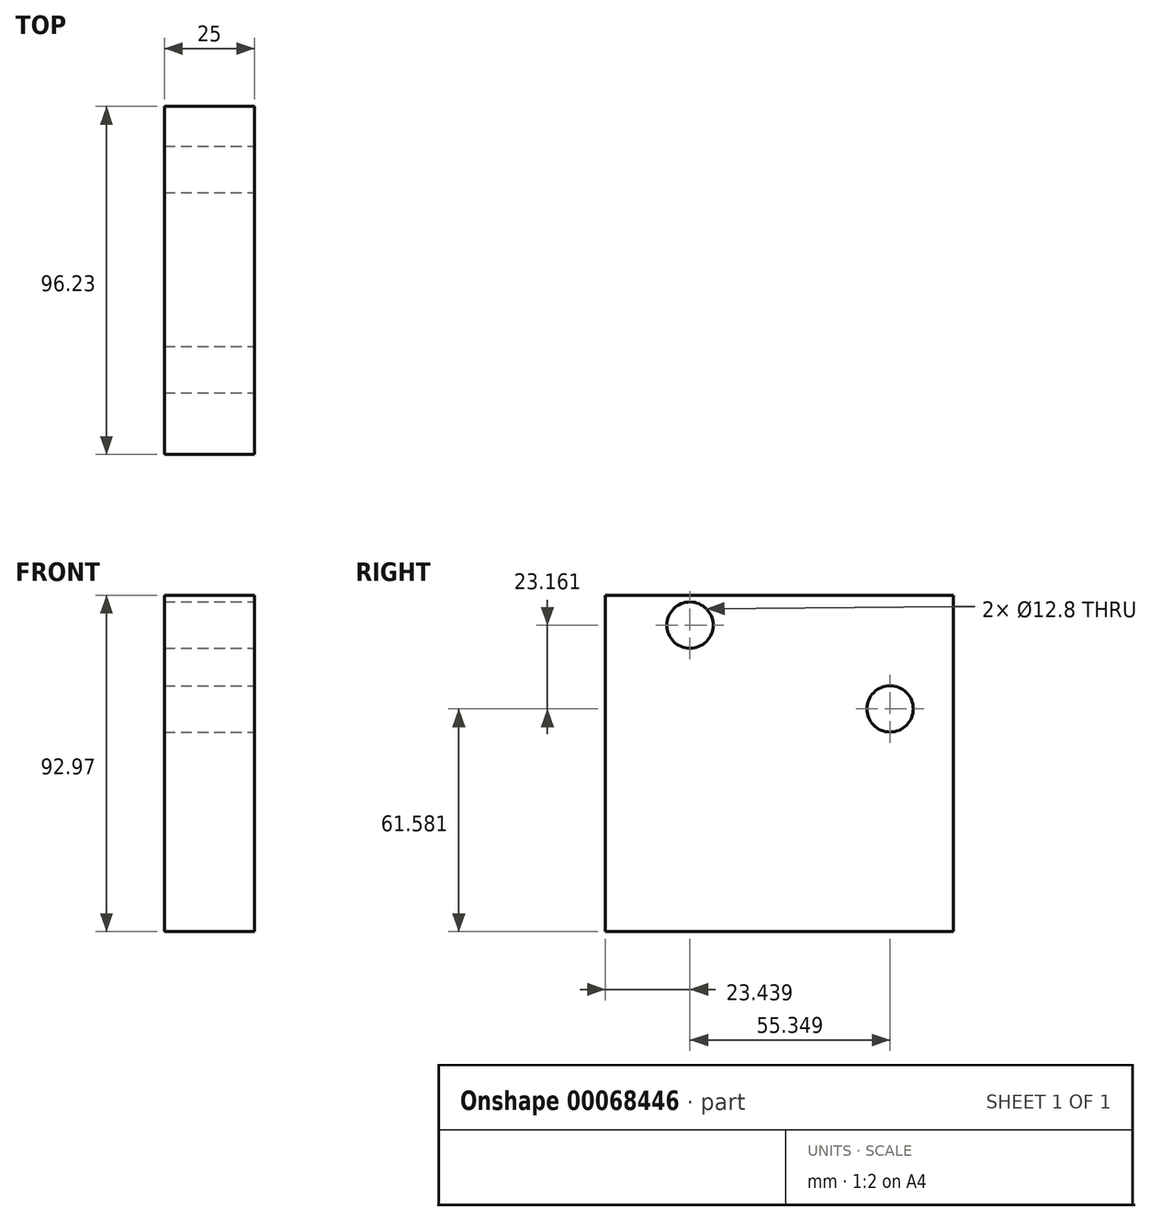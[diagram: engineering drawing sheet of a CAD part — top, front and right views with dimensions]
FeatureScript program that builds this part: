
annotation { "Feature Type Name" : "Feature", "Feature Type Description" : "" }
export const myFeature = defineFeature(function(context is Context, id is Id, definition is map)
    precondition{}
    {
        {
            var Q0;
            Q0=qCreatedBy(makeId("Right.planeOp"),FACE);
            var sketch = newSketch(context, id + "F0", { "sketchPlane" : qUnion([Q0])});
            skLineSegment(sketch, "E0.bottom", {"start": v(-50, 42.6) * mm, "end": v(46.23, 42.6) * mm});
            skLineSegment(sketch, "E0.top", {"start": v(-50, -50.37) * mm, "end": v(46.23, -50.37) * mm});
            skLineSegment(sketch, "E0.left", {"start": v(-50, 42.6) * mm, "end": v(-50, -50.37) * mm});
            skLineSegment(sketch, "E0.right", {"start": v(46.23, 42.6) * mm, "end": v(46.23, -50.37) * mm});
            skSolve(sketch);
        }
        {
            var Q0;
            Q0=makeQuery(id+"F0.imprint","IMPRINT",FACE,{"disambiguationData":[TD([[makeQuery(id+"F0.imprint","IMPRINT",EDGE,{"derivedFrom":sQuery(id+"F0.wireOp",EDGE,"E0.bottom")}),-1.0]])]});
            extrude(context, id + "F1", {"entities" : qUnion([Q0]), "depth" : 25 * mm});
        }
        {
            var Q0;
            Q0=makeQuery(id+"F1.opExtrude","CAP_FACE",FACE,{"disambiguationData":[OSD([sQuery(id+"F0.wireOp",EDGE,"E0.bottom"),sQuery(id+"F0.wireOp",EDGE,"E0.top"),sQuery(id+"F0.wireOp",EDGE,"E0.left"),sQuery(id+"F0.wireOp",EDGE,"E0.right")])],"isStart":false});
            var sketch = newSketch(context, id + "F2", { "sketchPlane" : qUnion([Q0])});
            skLineSegment(sketch, "E1", {"start": v(-26.56, 34.37) * mm, "end": v(28.79, 11.21) * mm});
            skLineSegment(sketch, "E2", {"start": v(-50, -50.37) * mm, "end": v(28.79, 11.21) * mm});
            skSolve(sketch);
        }
        {
            var Q0;
            Q0=sQuery(id+"F2.wireOp",VERTEX,"E1.start");
            var Q1;
            Q1=sQuery(id+"F2.wireOp",VERTEX,"E2.end");
            var Q2;
            Q2=makeQuery(id+"F1.opExtrude","SWEPT_BODY",BODY,{"disambiguationData":[OSD([sQuery(id+"F0.wireOp",EDGE,"E0.bottom"),sQuery(id+"F0.wireOp",EDGE,"E0.top"),sQuery(id+"F0.wireOp",EDGE,"E0.left"),sQuery(id+"F0.wireOp",EDGE,"E0.right")])]});
            hole(context, id + "F3", {"style" : HoleStyle.SIMPLE, "endStyle" : HoleEndStyle.THROUGH, "standardTappedOrClearance" : lookupTablePath({ "standard" : "ISO", "engagement" : "75%", "pitch" : "1.25 mm", "size" : "M14", "type" : "Tapped" }), "standardBlindInLast" : lookupTablePath({ "standard" : "ISO", "engagement" : "75%", "pitch" : "1.25 mm", "size" : "M14", "type" : "Tapped" }), "holeDiameter" : 12.8 * mm, "locations" : qUnion([Q0, Q1]), "scope" : qUnion([Q2]), "isTappedThrough" : true, "majorDiameter" : 14 * mm, "showTappedDepth" : true});
        }
    });
